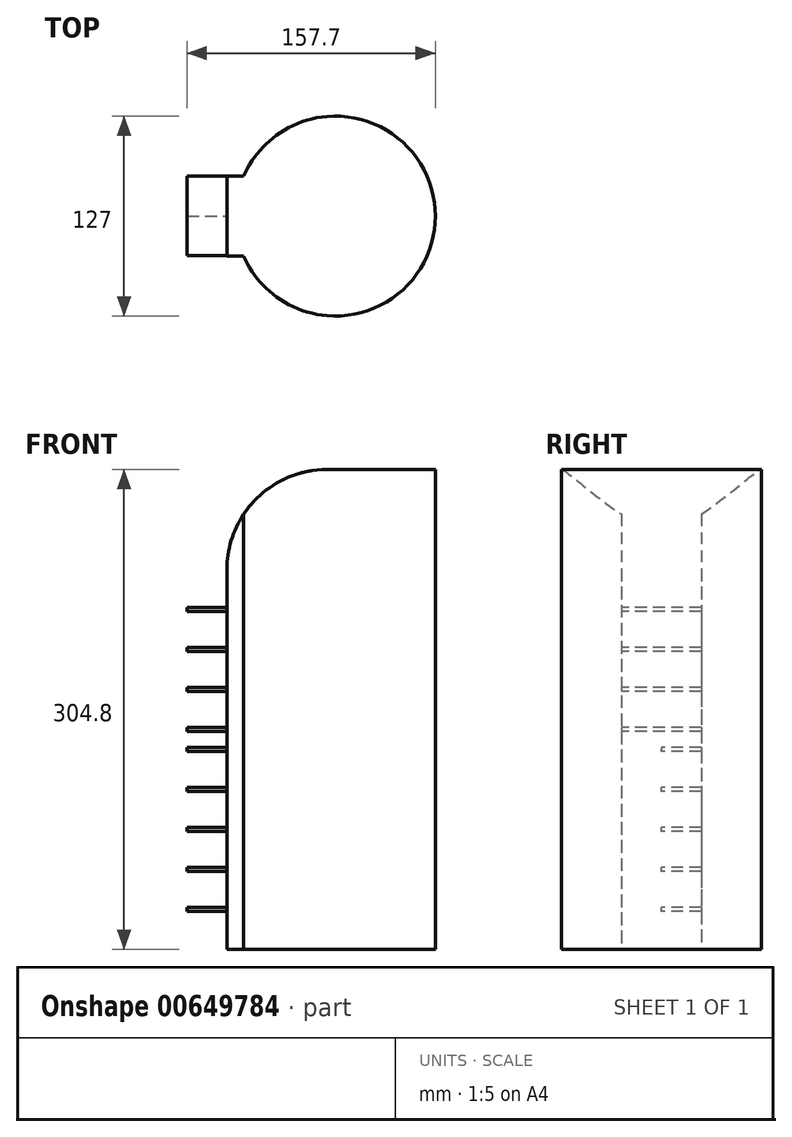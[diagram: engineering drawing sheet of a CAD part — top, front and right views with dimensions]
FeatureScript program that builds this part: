
annotation { "Feature Type Name" : "Feature", "Feature Type Description" : "" }
export const myFeature = defineFeature(function(context is Context, id is Id, definition is map)
    precondition{}
    {
        {
            var Q0;
            Q0=qCreatedBy(makeId("Top.planeOp"),FACE);
            var sketch = newSketch(context, id + "F0", { "sketchPlane" : qUnion([Q0])});
            skArc(sketch, "E0", {"start": v(-58.2, -25.4) * mm, "mid": v(63.5, 0) * mm, "end": v(-58.2, 25.4) * mm});
            skLineSegment(sketch, "E1.bottom", {"start": v(-58.2, 25.4) * mm, "end": v(-68.8, 25.4) * mm});
            skLineSegment(sketch, "E1.top", {"start": v(-58.2, -25.4) * mm, "end": v(-68.8, -25.4) * mm});
            skLineSegment(sketch, "E1.right", {"start": v(-68.8, 25.4) * mm, "end": v(-68.8, -25.4) * mm});
            skPoint(sketch, "E1.middle", {"position": v(-63.5, 0) * mm});
            skSolve(sketch);
        }
        {
            var Q0;
            Q0 = qSketchRegion(id + "F0", true);
            extrude(context, id + "F1", {"entities" : qUnion([Q0]), "depth" : 304.8 * mm, "offsetDistance" : 25.4 * mm});
        }
        {
            var Q0;
            Q0=makeQuery(id+"F1.opExtrude","CAP_EDGE",EDGE,{"disambiguationData":[OSD([sQuery(id+"F0.wireOp",EDGE,"E1.right")])],"isStart":false});
            fillet(context, id + "F2", {"entities" : qUnion([Q0]), "radius" : 63.5 * mm, "tangentPropagation" : true, "allowEdgeOverflow" : false});
        }
        {
            var Q0;
            Q0=makeQuery(id+"F1.opExtrude","SWEPT_FACE",FACE,{"disambiguationData":[OSD([sQuery(id+"F0.wireOp",EDGE,"E1.right")])]});
            var sketch = newSketch(context, id + "F3", { "sketchPlane" : qUnion([Q0])});
            skLineSegment(sketch, "E2.bottom", {"start": v(-25.4, 0) * mm, "end": v(25.4, 0) * mm});
            skLineSegment(sketch, "E2.top", {"start": v(-25.59, 241.3) * mm, "end": v(25.4, 241.3) * mm});
            skLineSegment(sketch, "E2.right", {"start": v(25.4, 0) * mm, "end": v(25.4, 241.3) * mm});
            skLineSegment(sketch, "E3", {"start": v(-0.1, 241.3) * mm, "end": v(-0.1, 215.9) * mm});
            skLineSegment(sketch, "E4", {"start": v(0, 0) * mm, "end": v(0, 25.4) * mm});
            skLineSegment(sketch, "E5", {"start": v(-0.1, 215.9) * mm, "end": v(-0.1, 190.5) * mm});
            skLineSegment(sketch, "E6", {"start": v(0, 25.4) * mm, "end": v(0, 50.8) * mm});
            skLineSegment(sketch, "E7", {"start": v(-0.1, 190.5) * mm, "end": v(-0.1, 165.1) * mm});
            skLineSegment(sketch, "E8", {"start": v(0, 50.8) * mm, "end": v(0, 76.2) * mm});
            skLineSegment(sketch, "E9", {"start": v(-0.1, 165.1) * mm, "end": v(-0.1, 139.7) * mm});
            skLineSegment(sketch, "E10", {"start": v(0, 76.2) * mm, "end": v(0, 101.6) * mm});
            skLineSegment(sketch, "E11", {"start": v(0, 101.6) * mm, "end": v(0, 127) * mm});
            skLineSegment(sketch, "E12", {"start": v(-0.1, 139.7) * mm, "end": v(0, 127) * mm});
            skLineSegment(sketch, "E13.bottom", {"start": v(-25.4, 26.67) * mm, "end": v(25.4, 26.67) * mm});
            skLineSegment(sketch, "E13.top", {"start": v(-25.4, 24.13) * mm, "end": v(25.4, 24.13) * mm});
            skLineSegment(sketch, "E13.left", {"start": v(-25.4, 26.67) * mm, "end": v(-25.4, 24.13) * mm});
            skLineSegment(sketch, "E13.right", {"start": v(25.4, 26.67) * mm, "end": v(25.4, 24.13) * mm});
            skPoint(sketch, "E13.middle", {"position": v(0, 25.4) * mm});
            skLineSegment(sketch, "E14.bottom", {"start": v(-25.4, 52.07) * mm, "end": v(25.4, 52.07) * mm});
            skLineSegment(sketch, "E14.top", {"start": v(-25.4, 49.53) * mm, "end": v(25.4, 49.53) * mm});
            skLineSegment(sketch, "E14.left", {"start": v(-25.4, 52.07) * mm, "end": v(-25.4, 49.53) * mm});
            skLineSegment(sketch, "E14.right", {"start": v(25.4, 52.07) * mm, "end": v(25.4, 49.53) * mm});
            skPoint(sketch, "E14.middle", {"position": v(0, 50.8) * mm});
            skLineSegment(sketch, "E15.bottom", {"start": v(-25.4, 77.47) * mm, "end": v(25.4, 77.47) * mm});
            skLineSegment(sketch, "E15.top", {"start": v(-25.4, 74.93) * mm, "end": v(25.4, 74.93) * mm});
            skLineSegment(sketch, "E15.left", {"start": v(-25.4, 77.47) * mm, "end": v(-25.4, 74.93) * mm});
            skLineSegment(sketch, "E15.right", {"start": v(25.4, 77.47) * mm, "end": v(25.4, 74.93) * mm});
            skPoint(sketch, "E15.middle", {"position": v(0, 76.2) * mm});
            skLineSegment(sketch, "E16.bottom", {"start": v(-25.4, 102.87) * mm, "end": v(25.4, 102.87) * mm});
            skLineSegment(sketch, "E16.top", {"start": v(-25.4, 100.33) * mm, "end": v(25.4, 100.33) * mm});
            skLineSegment(sketch, "E16.left", {"start": v(-25.4, 102.87) * mm, "end": v(-25.4, 100.33) * mm});
            skLineSegment(sketch, "E16.right", {"start": v(25.4, 102.87) * mm, "end": v(25.4, 100.33) * mm});
            skPoint(sketch, "E16.middle", {"position": v(0, 101.6) * mm});
            skLineSegment(sketch, "E17.bottom", {"start": v(-25.4, 128.27) * mm, "end": v(25.4, 128.27) * mm});
            skLineSegment(sketch, "E17.top", {"start": v(-25.4, 125.73) * mm, "end": v(25.4, 125.73) * mm});
            skLineSegment(sketch, "E17.left", {"start": v(-25.4, 128.27) * mm, "end": v(-25.4, 125.73) * mm});
            skLineSegment(sketch, "E17.right", {"start": v(25.4, 128.27) * mm, "end": v(25.4, 125.73) * mm});
            skPoint(sketch, "E17.middle", {"position": v(0, 127) * mm});
            skLineSegment(sketch, "E18.bottom", {"start": v(-25.4, 140.97) * mm, "end": v(25.21, 140.97) * mm});
            skLineSegment(sketch, "E18.top", {"start": v(-25.4, 138.43) * mm, "end": v(25.21, 138.43) * mm});
            skLineSegment(sketch, "E18.left", {"start": v(-25.4, 140.97) * mm, "end": v(-25.4, 138.43) * mm});
            skLineSegment(sketch, "E18.right", {"start": v(25.21, 140.97) * mm, "end": v(25.21, 138.43) * mm});
            skPoint(sketch, "E18.middle", {"position": v(-0.1, 139.7) * mm});
            skLineSegment(sketch, "E19.bottom", {"start": v(-25.4, 166.37) * mm, "end": v(25.21, 166.37) * mm});
            skLineSegment(sketch, "E19.top", {"start": v(-25.4, 163.83) * mm, "end": v(25.21, 163.83) * mm});
            skLineSegment(sketch, "E19.left", {"start": v(-25.4, 166.37) * mm, "end": v(-25.4, 163.83) * mm});
            skLineSegment(sketch, "E19.right", {"start": v(25.21, 166.37) * mm, "end": v(25.21, 163.83) * mm});
            skPoint(sketch, "E19.middle", {"position": v(-0.1, 165.1) * mm});
            skLineSegment(sketch, "E20.bottom", {"start": v(-25.4, 191.77) * mm, "end": v(25.21, 191.77) * mm});
            skLineSegment(sketch, "E20.top", {"start": v(-25.4, 189.23) * mm, "end": v(25.21, 189.23) * mm});
            skLineSegment(sketch, "E20.left", {"start": v(-25.4, 191.77) * mm, "end": v(-25.4, 189.23) * mm});
            skLineSegment(sketch, "E20.right", {"start": v(25.21, 191.77) * mm, "end": v(25.21, 189.23) * mm});
            skPoint(sketch, "E20.middle", {"position": v(-0.1, 190.5) * mm});
            skLineSegment(sketch, "E21.bottom", {"start": v(-25.4, 217.17) * mm, "end": v(25.21, 217.17) * mm});
            skLineSegment(sketch, "E21.top", {"start": v(-25.4, 214.63) * mm, "end": v(25.21, 214.63) * mm});
            skLineSegment(sketch, "E21.left", {"start": v(-25.4, 217.17) * mm, "end": v(-25.4, 214.63) * mm});
            skLineSegment(sketch, "E21.right", {"start": v(25.21, 217.17) * mm, "end": v(25.21, 214.63) * mm});
            skPoint(sketch, "E21.middle", {"position": v(-0.1, 215.9) * mm});
            skSolve(sketch);
        }
        {
            var Q0;
            {var subQ0=sQuery(id+"F3.wireOp",EDGE,"E21.left");Q0=makeQuery(id+"F3.imprint","IMPRINT",FACE,{"disambiguationData":[TD([[makeQuery(id+"F3.imprint","IMPRINT",EDGE,{"derivedFrom":subQ0}),1.0]])]});}
            var Q1;
            {var subQ0=sQuery(id+"F3.wireOp",EDGE,"E21.right");Q1=makeQuery(id+"F3.imprint","IMPRINT",FACE,{"disambiguationData":[TD([[makeQuery(id+"F3.imprint","IMPRINT",EDGE,{"derivedFrom":subQ0}),-1.0]])]});}
            var Q2;
            {var subQ0=sQuery(id+"F3.wireOp",EDGE,"E20.right");Q2=makeQuery(id+"F3.imprint","IMPRINT",FACE,{"disambiguationData":[TD([[makeQuery(id+"F3.imprint","IMPRINT",EDGE,{"derivedFrom":subQ0}),-1.0]])]});}
            var Q3;
            {var subQ0=sQuery(id+"F3.wireOp",EDGE,"E20.left");Q3=makeQuery(id+"F3.imprint","IMPRINT",FACE,{"disambiguationData":[TD([[makeQuery(id+"F3.imprint","IMPRINT",EDGE,{"derivedFrom":subQ0}),1.0]])]});}
            var Q4;
            {var subQ0=sQuery(id+"F3.wireOp",EDGE,"E19.left");Q4=makeQuery(id+"F3.imprint","IMPRINT",FACE,{"disambiguationData":[TD([[makeQuery(id+"F3.imprint","IMPRINT",EDGE,{"derivedFrom":subQ0}),1.0]])]});}
            var Q5;
            {var subQ0=sQuery(id+"F3.wireOp",EDGE,"E19.right");Q5=makeQuery(id+"F3.imprint","IMPRINT",FACE,{"disambiguationData":[TD([[makeQuery(id+"F3.imprint","IMPRINT",EDGE,{"derivedFrom":subQ0}),-1.0]])]});}
            var Q6;
            {var subQ0=sQuery(id+"F3.wireOp",EDGE,"E17.left");Q6=makeQuery(id+"F3.imprint","IMPRINT",FACE,{"disambiguationData":[TD([[makeQuery(id+"F3.imprint","IMPRINT",EDGE,{"derivedFrom":subQ0}),1.0]])]});}
            var Q7;
            {var subQ0=sQuery(id+"F3.wireOp",EDGE,"E18.left");Q7=makeQuery(id+"F3.imprint","IMPRINT",FACE,{"disambiguationData":[TD([[makeQuery(id+"F3.imprint","IMPRINT",EDGE,{"derivedFrom":subQ0}),1.0]])]});}
            var Q8;
            {var subQ0=sQuery(id+"F3.wireOp",EDGE,"E18.right");Q8=makeQuery(id+"F3.imprint","IMPRINT",FACE,{"disambiguationData":[TD([[makeQuery(id+"F3.imprint","IMPRINT",EDGE,{"derivedFrom":subQ0}),-1.0]])]});}
            var Q9;
            {var subQ0=sQuery(id+"F3.wireOp",EDGE,"E17.right");Q9=makeQuery(id+"F3.imprint","IMPRINT",FACE,{"disambiguationData":[TD([[makeQuery(id+"F3.imprint","IMPRINT",EDGE,{"derivedFrom":subQ0}),-1.0]])]});}
            var Q10;
            {var subQ0=sQuery(id+"F3.wireOp",EDGE,"E16.left");Q10=makeQuery(id+"F3.imprint","IMPRINT",FACE,{"disambiguationData":[TD([[makeQuery(id+"F3.imprint","IMPRINT",EDGE,{"derivedFrom":subQ0}),1.0]])]});}
            var Q11;
            {var subQ0=sQuery(id+"F3.wireOp",EDGE,"E16.right");Q11=makeQuery(id+"F3.imprint","IMPRINT",FACE,{"disambiguationData":[TD([[makeQuery(id+"F3.imprint","IMPRINT",EDGE,{"derivedFrom":subQ0}),-1.0]])]});}
            var Q12;
            {var subQ0=sQuery(id+"F3.wireOp",EDGE,"E15.left");Q12=makeQuery(id+"F3.imprint","IMPRINT",FACE,{"disambiguationData":[TD([[makeQuery(id+"F3.imprint","IMPRINT",EDGE,{"derivedFrom":subQ0}),1.0]])]});}
            var Q13;
            {var subQ0=sQuery(id+"F3.wireOp",EDGE,"E14.left");Q13=makeQuery(id+"F3.imprint","IMPRINT",FACE,{"disambiguationData":[TD([[makeQuery(id+"F3.imprint","IMPRINT",EDGE,{"derivedFrom":subQ0}),1.0]])]});}
            var Q14;
            {var subQ0=sQuery(id+"F3.wireOp",EDGE,"E14.right");Q14=makeQuery(id+"F3.imprint","IMPRINT",FACE,{"disambiguationData":[TD([[makeQuery(id+"F3.imprint","IMPRINT",EDGE,{"derivedFrom":subQ0}),-1.0]])]});}
            var Q15;
            {var subQ0=sQuery(id+"F3.wireOp",EDGE,"E15.right");Q15=makeQuery(id+"F3.imprint","IMPRINT",FACE,{"disambiguationData":[TD([[makeQuery(id+"F3.imprint","IMPRINT",EDGE,{"derivedFrom":subQ0}),-1.0]])]});}
            var Q16;
            {var subQ0=sQuery(id+"F3.wireOp",EDGE,"E13.left");Q16=makeQuery(id+"F3.imprint","IMPRINT",FACE,{"disambiguationData":[TD([[makeQuery(id+"F3.imprint","IMPRINT",EDGE,{"derivedFrom":subQ0}),1.0]])]});}
            var Q17;
            {var subQ0=sQuery(id+"F3.wireOp",EDGE,"E13.right");Q17=makeQuery(id+"F3.imprint","IMPRINT",FACE,{"disambiguationData":[TD([[makeQuery(id+"F3.imprint","IMPRINT",EDGE,{"derivedFrom":subQ0}),-1.0]])]});}
            extrude(context, id + "F4", {"entities" : qUnion([Q0, Q1, Q2, Q3, Q4, Q5, Q6, Q7, Q8, Q9, Q10, Q11, Q12, Q13, Q14, Q15, Q16, Q17]), "operationType" : NewBodyOperationType.ADD, "depth" : 25.4 * mm, "offsetDistance" : 25.4 * mm});
        }
    });
